annotation { "Feature Type Name" : "Feature", "Feature Type Description" : "" }
export const myFeature = defineFeature(function(context is Context, id is Id, definition is map)
    precondition{}
    {
        {
            var Q0;
            Q0=qCreatedBy(makeId("Top.planeOp"),FACE);
            var sketch = newSketch(context, id + "F0", { "sketchPlane" : qUnion([Q0])});
            skLineSegment(sketch, "E0", {"start": v(-51.94, 30.38) * mm, "end": v(-44.76, 20.97) * mm});
            skFitSpline(sketch, "E1", {"points": [v(-44.76, 20.97) * mm, v(-44.39, 20.47) * mm, v(-44.22, 19.47) * mm, v(-46.32, 14.33) * mm, v(-46.52, 13.88) * mm, v(-47.24, 13.24) * mm], "startDerivative": vector(2.86, -3.64) * mm, "endDerivative": vector(-5.31, -4.28) * mm});
            skLineSegment(sketch, "E2", {"start": v(-47.24, 13.24) * mm, "end": v(-59.29, 11.1) * mm});
            skFitSpline(sketch, "E3", {"points": [v(-59.29, 11.1) * mm, v(-59.99, 10.84) * mm, v(-60.57, 10.31) * mm, v(-60.93, 9.87) * mm, v(-61.27, 6.94) * mm], "startDerivative": vector(-3.55, -0.83) * mm, "endDerivative": vector(-0.45, -8.94) * mm});
            skLineSegment(sketch, "E4", {"start": v(-61.27, 6.94) * mm, "end": v(-61.97, -0.64) * mm});
            skPoint(sketch, "E5.2.internal.snap0", {"position": v(-61.97, -2.36) * mm});
            skFitSpline(sketch, "E5", {"points": [v(-61.97, -0.64) * mm, v(-61.97, -1.78) * mm, v(-61.75, -2.36) * mm, v(-50.69, -6.35) * mm, v(-48.96, -7.57) * mm, v(-47.82, -13.68) * mm, v(-47.97, -14.98) * mm, v(-54.87, -21.25) * mm, v(-57.29, -23.57) * mm, v(-57.67, -25.21) * mm, v(-52.6, -35.06) * mm, v(-52.2, -35.57) * mm, v(-51.5, -35.66) * mm, v(-39.96, -33.15) * mm, v(-38.3, -33.12) * mm, v(-33.2, -38.23) * mm, v(-33.29, -41.11) * mm, v(-35.98, -51.78) * mm, v(-34.74, -53.2) * mm, v(-26.08, -58.06) * mm, v(-24.3, -57.8) * mm, v(-16, -49.57) * mm, v(-12.46, -49.4) * mm, v(-7.95, -50.46) * mm, v(-3.8, -62.22) * mm, v(0.8, -64.16) * mm, v(9.62, -63.4) * mm], "startDerivative": vector(2, -66.55) * mm, "endDerivative": vector(176.75, 21.12) * mm});
            skFitSpline(sketch, "E6", {"points": [v(9.62, -63.4) * mm, v(10.52, -62.71) * mm, v(13.2, -49.37) * mm, v(14.78, -48.21) * mm, v(19.6, -46.52) * mm, v(21.92, -48) * mm, v(29.32, -54.71) * mm, v(31.86, -54.89) * mm, v(41.98, -47.3) * mm, v(41.85, -44.9) * mm, v(37.2, -33.9) * mm, v(37.95, -31.67) * mm, v(40.58, -28.45) * mm, v(43.38, -28.35) * mm, v(53.44, -29.43) * mm, v(55.09, -28.64) * mm, v(59.01, -17.27) * mm, v(58.22, -15.68) * mm, v(47.92, -8.27) * mm, v(47.55, -7.1) * mm, v(47.83, -2.84) * mm, v(48.68, -1.8) * mm, v(59.4, 3.55) * mm, v(60.44, 4.97) * mm, v(57.68, 17.84) * mm, v(56.14, 18.39) * mm, v(44.05, 18.97) * mm, v(42.8, 20.35) * mm, v(41.21, 23.24) * mm, v(42.55, 26.2) * mm, v(47.83, 34.99) * mm, v(46.52, 37.96) * mm, v(38.24, 46.1) * mm, v(35.06, 45.48) * mm, v(26.5, 40.1) * mm, v(21.54, 41.82) * mm, v(21.23, 45.93) * mm, v(20.86, 55.38) * mm, v(7.43, 59.98) * mm, v(0.96, 49.66) * mm, v(-1.53, 47.3) * mm, v(-5.01, 47.17) * mm, v(-12.1, 57.12) * mm, v(-16.58, 57.74) * mm, v(-27.65, 54.26) * mm, v(-27.9, 51.9) * mm, v(-26.53, 41.08) * mm, v(-29.64, 37.97) * mm, v(-31.13, 36.97) * mm, v(-43.07, 41.82) * mm, v(-46.43, 40.33) * mm, v(-51.28, 33.74) * mm, v(-52.49, 32.15) * mm, v(-51.94, 30.38) * mm], "startDerivative": vector(108.53, 13.76) * mm, "endDerivative": vector(83.84, -176.62) * mm});
            skSolve(sketch);
        }
        {
            var Q0;
            Q0 = qSketchRegion(id + "F0", true);
            extrude(context, id + "F1", {"entities" : qUnion([Q0]), "depth" : 13.97 * mm, "offsetDistance" : 25.4 * mm});
        }
        {
            var Q0;
            Q0=makeQuery(id+"F1.opExtrude","CAP_FACE",FACE,{"disambiguationData":[OSD([sQuery(id+"F0.wireOp",EDGE,"E0"),sQuery(id+"F0.wireOp",EDGE,"E1"),sQuery(id+"F0.wireOp",EDGE,"E2"),sQuery(id+"F0.wireOp",EDGE,"E3"),sQuery(id+"F0.wireOp",EDGE,"E4"),sQuery(id+"F0.wireOp",EDGE,"E5"),sQuery(id+"F0.wireOp",EDGE,"E6")])],"isStart":false});
            var sketch = newSketch(context, id + "F2", { "sketchPlane" : qUnion([Q0])});
            skText(sketch, "E7", { "text": "DEEP FUEL\nNUTRITION", "fontName": "OpenSans-Bold.ttf"});
            const initialGuessF2  = {"E7": [-0.03098, 0.00595, 1, 0, 0.00817]};
            skSetInitialGuess(sketch, initialGuessF2);
            skSolve(sketch);
        }
        {
            var Q0;
            Q0 = qSketchRegion(id + "F2", true);
            extrude(context, id + "F3", {"entities" : qUnion([Q0]), "operationType" : NewBodyOperationType.ADD, "depth" : 1.27 * mm, "offsetDistance" : 25.4 * mm});
        }
    });